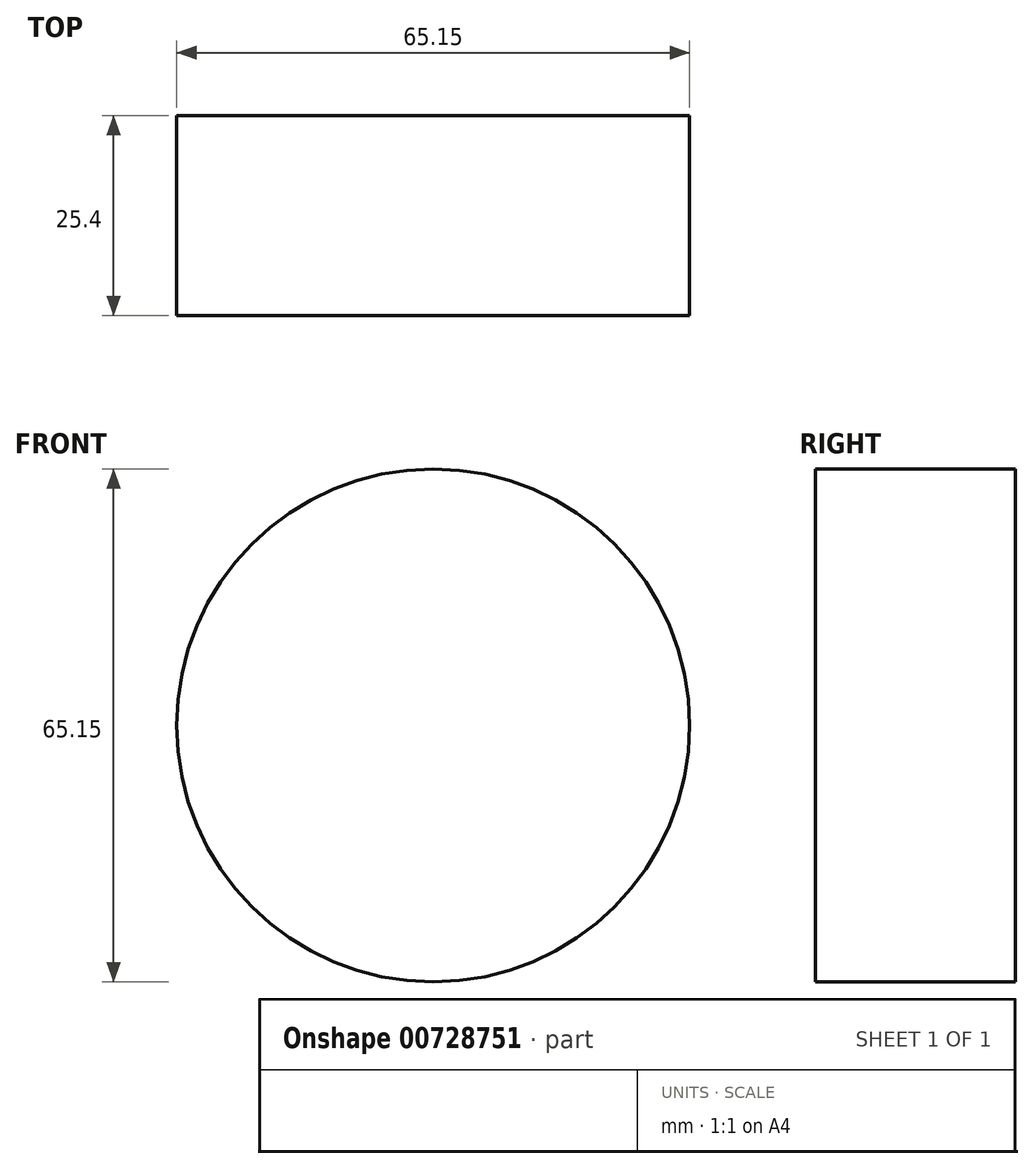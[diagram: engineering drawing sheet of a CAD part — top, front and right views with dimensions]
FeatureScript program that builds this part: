
annotation { "Feature Type Name" : "Feature", "Feature Type Description" : "" }
export const myFeature = defineFeature(function(context is Context, id is Id, definition is map)
    precondition{}
    {
        {
            var Q0;
            Q0=qCreatedBy(makeId("Front.planeOp"),FACE);
            var sketch = newSketch(context, id + "F0", { "sketchPlane" : qUnion([Q0])});
            skCircle(sketch, "E0", {"center": v(18.23, 27) * mm, "radius": 32.58 * mm});
            skSolve(sketch);
        }
        {
            var Q0;
            Q0=makeQuery(id+"F0.imprint","IMPRINT",FACE,{"disambiguationData":[TD([[makeQuery(id+"F0.imprint","IMPRINT",EDGE,{"derivedFrom":sQuery(id+"F0.wireOp",EDGE,"E0")}),1.0]])]});
            extrude(context, id + "F1", {"entities" : qUnion([Q0]), "depth" : 25.4 * mm, "offsetDistance" : 25.4 * mm});
        }
    });
